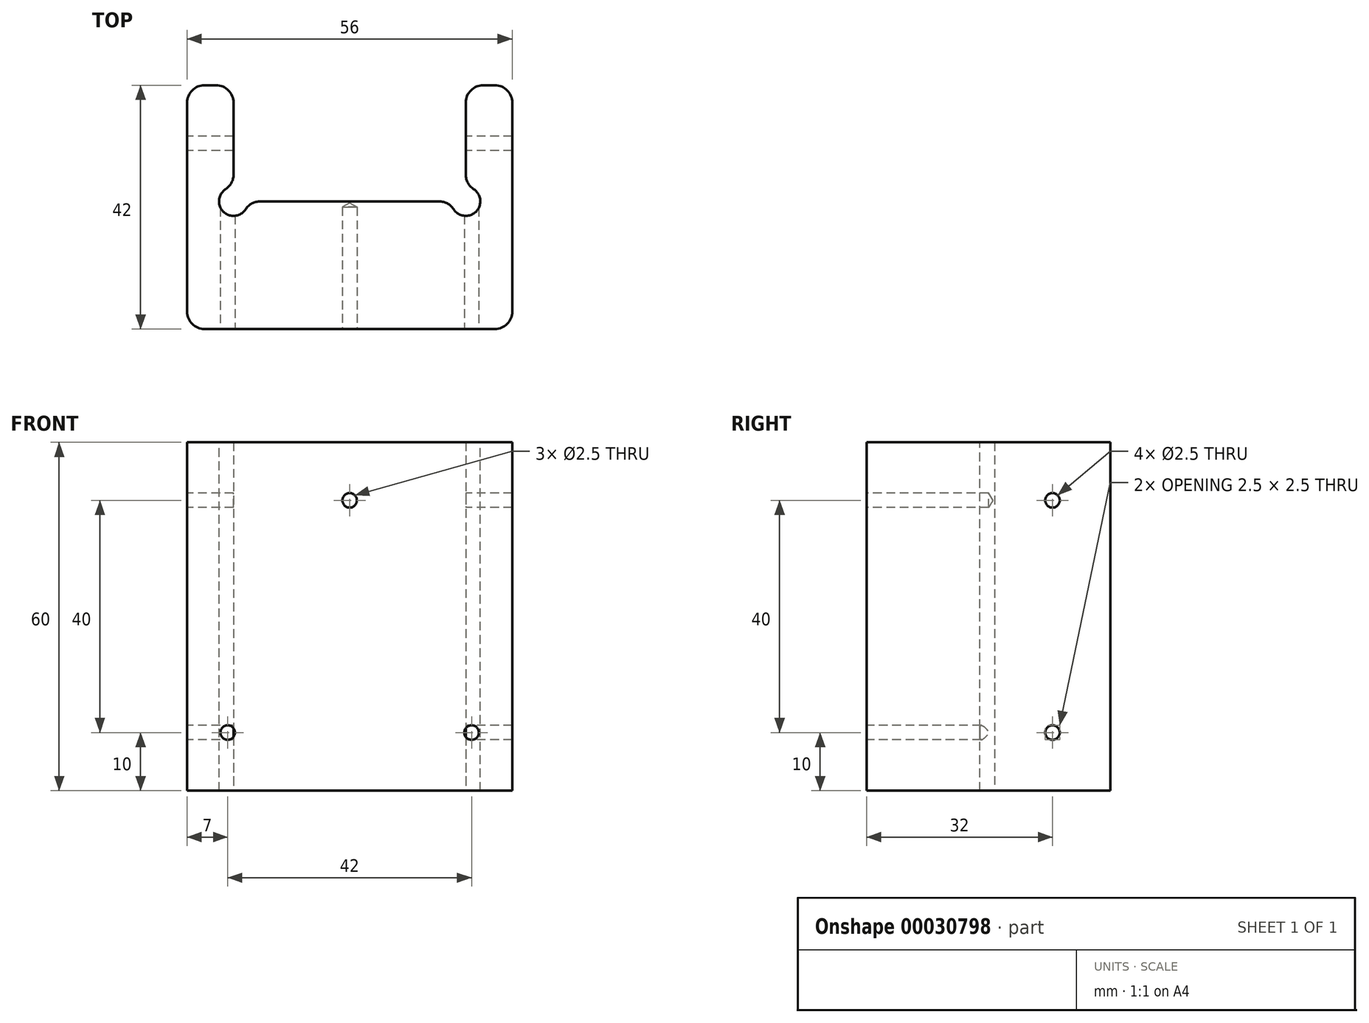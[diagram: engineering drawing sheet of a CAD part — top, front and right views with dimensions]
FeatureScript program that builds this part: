
annotation { "Feature Type Name" : "Feature", "Feature Type Description" : "" }
export const myFeature = defineFeature(function(context is Context, id is Id, definition is map)
    precondition{}
    {
        {
            var Q0;
            Q0=qCreatedBy(makeId("Top.planeOp"),FACE);
            var sketch = newSketch(context, id + "F0", { "sketchPlane" : qUnion([Q0])});
            skLineSegment(sketch, "E0.rect.bottom", {"start": v(-28, 21) * mm, "end": v(-20, 21) * mm});
            skLineSegment(sketch, "E0.rect.top", {"start": v(-28, -21) * mm, "end": v(28, -21) * mm});
            skLineSegment(sketch, "E0.rect.left", {"start": v(-28, 21) * mm, "end": v(-28, -21) * mm});
            skLineSegment(sketch, "E0.rect.right", {"start": v(28, 21) * mm, "end": v(28, -21) * mm});
            skPoint(sketch, "E0.rect.middle", {"position": v(0, 0) * mm});
            skLineSegment(sketch, "E1", {"start": v(-20, 21) * mm, "end": v(-20, 1) * mm});
            skLineSegment(sketch, "E2", {"start": v(-20, 1) * mm, "end": v(20, 1) * mm});
            skLineSegment(sketch, "E3", {"start": v(20, 1) * mm, "end": v(20, 21) * mm});
            skLineSegment(sketch, "E4.trimOffspring", {"start": v(20, 21) * mm, "end": v(28, 21) * mm});
            skSolve(sketch);
        }
        {
            var Q0;
            Q0 = qSketchRegion(id + "F0", true);
            extrude(context, id + "F1", {"entities" : qUnion([Q0]), "endBound" : BoundingType.SYMMETRIC, "depth" : 60 * mm});
        }
        {
            var Q0;
            Q0=makeQuery(id+"F1.opExtrude","SWEPT_FACE",FACE,{"disambiguationData":[OSD([sQuery(id+"F0.wireOp",EDGE,"E0.rect.left")])]});
            var sketch = newSketch(context, id + "F2", { "sketchPlane" : qUnion([Q0])});
            skPoint(sketch, "E5", {"position": v(-11, 20) * mm});
            skPoint(sketch, "E6", {"position": v(-11, -20) * mm});
            skLineSegment(sketch, "E7", {"start": v(-11, 20) * mm, "end": v(-11, -20) * mm, "construction": true});
            skLineSegment(sketch, "E8", {"start": v(-11, 0) * mm, "end": v(0, 0) * mm, "construction": true});
            skSolve(sketch);
        }
        {
            var Q0;
            Q0=sQuery(id+"F2.wireOp",VERTEX,"E5");
            var Q1;
            Q1=sQuery(id+"F2.wireOp",VERTEX,"E6");
            var Q2;
            Q2=makeQuery(id+"F1.opExtrude","SWEPT_BODY",BODY,{"disambiguationData":[OSD([sQuery(id+"F0.wireOp",EDGE,"E0.rect.bottom"),sQuery(id+"F0.wireOp",EDGE,"E0.rect.top"),sQuery(id+"F0.wireOp",EDGE,"E0.rect.left"),sQuery(id+"F0.wireOp",EDGE,"E0.rect.right"),sQuery(id+"F0.wireOp",EDGE,"E1"),sQuery(id+"F0.wireOp",EDGE,"E2"),sQuery(id+"F0.wireOp",EDGE,"E3"),sQuery(id+"F0.wireOp",EDGE,"E4.trimOffspring")])]});
            hole(context, id + "F3", {"style" : HoleStyle.SIMPLE, "holeDiameter" : 2.5 * mm, "endStyle" : HoleEndStyle.THROUGH, "locations" : qUnion([Q0, Q1]), "scope" : qUnion([Q2])});
        }
        {
            var Q0;
            Q0=makeQuery(id+"F1.opExtrude","SWEPT_FACE",FACE,{"disambiguationData":[OSD([sQuery(id+"F0.wireOp",EDGE,"E0.rect.top")])]});
            var sketch = newSketch(context, id + "F4", { "sketchPlane" : qUnion([Q0])});
            skPoint(sketch, "E9", {"position": v(0, 20) * mm});
            skPoint(sketch, "E10", {"position": v(-21, -20) * mm});
            skPoint(sketch, "E11", {"position": v(21, -20) * mm});
            skLineSegment(sketch, "E12", {"start": v(0, 20) * mm, "end": v(0, 0) * mm, "construction": true});
            skLineSegment(sketch, "E13", {"start": v(0, 0) * mm, "end": v(-21, -20) * mm, "construction": true});
            skLineSegment(sketch, "E14", {"start": v(0, 0) * mm, "end": v(21, -20) * mm, "construction": true});
            skLineSegment(sketch, "E15", {"start": v(0, 20) * mm, "end": v(-21, -20) * mm, "construction": true});
            skLineSegment(sketch, "E16", {"start": v(-21, -20) * mm, "end": v(21, -20) * mm, "construction": true});
            skLineSegment(sketch, "E17", {"start": v(21, -20) * mm, "end": v(0, 20) * mm, "construction": true});
            skLineSegment(sketch, "E18", {"start": v(0, 0) * mm, "end": v(0, -20) * mm, "construction": true});
            skSolve(sketch);
        }
        {
            var Q0;
            Q0=sQuery(id+"F4.wireOp",VERTEX,"E9");
            var Q1;
            Q1=sQuery(id+"F4.wireOp",VERTEX,"E10");
            var Q2;
            Q2=sQuery(id+"F4.wireOp",VERTEX,"E11");
            var Q3;
            Q3=makeQuery(id+"F1.opExtrude","SWEPT_BODY",BODY,{"disambiguationData":[OSD([sQuery(id+"F0.wireOp",EDGE,"E0.rect.bottom"),sQuery(id+"F0.wireOp",EDGE,"E0.rect.top"),sQuery(id+"F0.wireOp",EDGE,"E0.rect.left"),sQuery(id+"F0.wireOp",EDGE,"E0.rect.right"),sQuery(id+"F0.wireOp",EDGE,"E1"),sQuery(id+"F0.wireOp",EDGE,"E2"),sQuery(id+"F0.wireOp",EDGE,"E3"),sQuery(id+"F0.wireOp",EDGE,"E4.trimOffspring")])]});
            hole(context, id + "F5", {"style" : HoleStyle.SIMPLE, "holeDiameter" : 2.5 * mm, "endStyle" : HoleEndStyle.BLIND, "holeDepth" : 21 * mm, "locations" : qUnion([Q0, Q1, Q2]), "scope" : qUnion([Q3])});
        }
        {
            var Q0;
            Q0=makeQuery(id+"F1.opExtrude","SWEPT_EDGE",EDGE,{"disambiguationData":[OSD([sQuery(id+"F0.wireOp",EDGE,"E0.rect.top"),sQuery(id+"F0.wireOp",EDGE,"E0.rect.left")])]});
            var Q1;
            Q1=makeQuery(id+"F1.opExtrude","SWEPT_EDGE",EDGE,{"disambiguationData":[OSD([sQuery(id+"F0.wireOp",EDGE,"E0.rect.top"),sQuery(id+"F0.wireOp",EDGE,"E0.rect.right")])]});
            var Q2;
            Q2=makeQuery(id+"F1.opExtrude","SWEPT_EDGE",EDGE,{"disambiguationData":[OSD([sQuery(id+"F0.wireOp",EDGE,"E0.rect.bottom"),sQuery(id+"F0.wireOp",EDGE,"E0.rect.left")])]});
            var Q3;
            Q3=makeQuery(id+"F1.opExtrude","SWEPT_EDGE",EDGE,{"disambiguationData":[OSD([sQuery(id+"F0.wireOp",EDGE,"E0.rect.bottom"),sQuery(id+"F0.wireOp",EDGE,"E1")])]});
            var Q4;
            Q4=makeQuery(id+"F1.opExtrude","SWEPT_EDGE",EDGE,{"disambiguationData":[OSD([sQuery(id+"F0.wireOp",EDGE,"E3"),sQuery(id+"F0.wireOp",EDGE,"E4.trimOffspring")])]});
            var Q5;
            Q5=makeQuery(id+"F1.opExtrude","SWEPT_EDGE",EDGE,{"disambiguationData":[OSD([sQuery(id+"F0.wireOp",EDGE,"E0.rect.right"),sQuery(id+"F0.wireOp",EDGE,"E4.trimOffspring")])]});
            fillet(context, id + "F6", {"entities" : qUnion([Q0, Q1, Q2, Q3, Q4, Q5]), "radius" : 3 * mm, "tangentPropagation" : true, "allowEdgeOverflow" : false});
        }
        {
            var Q0;
            Q0=makeQuery(id+"F1.opExtrude","CAP_FACE",FACE,{"disambiguationData":[OSD([sQuery(id+"F0.wireOp",EDGE,"E0.rect.bottom"),sQuery(id+"F0.wireOp",EDGE,"E0.rect.top"),sQuery(id+"F0.wireOp",EDGE,"E0.rect.left"),sQuery(id+"F0.wireOp",EDGE,"E0.rect.right"),sQuery(id+"F0.wireOp",EDGE,"E1"),sQuery(id+"F0.wireOp",EDGE,"E2"),sQuery(id+"F0.wireOp",EDGE,"E3"),sQuery(id+"F0.wireOp",EDGE,"E4.trimOffspring")])],"isStart":false});
            var sketch = newSketch(context, id + "F7", { "sketchPlane" : qUnion([Q0])});
            skCircle(sketch, "E19", {"center": v(-20, 1) * mm, "radius": 2.5 * mm});
            skCircle(sketch, "E20", {"center": v(20, 1) * mm, "radius": 2.5 * mm});
            skSolve(sketch);
        }
        {
            var Q0;
            Q0 = qSketchRegion(id + "F7", true);
            extrude(context, id + "F8", {"entities" : qUnion([Q0]), "operationType" : NewBodyOperationType.REMOVE, "endBound" : BoundingType.THROUGH_ALL, "oppositeDirection" : true, "depth" : 25 * mm});
        }
        {
            var Q0;
            Q0=makeQuery(id+"F8.boolean.opBoolean","INTERSECT",EDGE,{"derivedFrom":[makeQuery(id+"F1.opExtrude","SWEPT_FACE",FACE,{"disambiguationData":[OSD([sQuery(id+"F0.wireOp",EDGE,"E2")])]}),makeQuery(id+"F8.opExtrude","SWEPT_FACE",FACE,{"disambiguationData":[OSD([sQuery(id+"F7.wireOp",EDGE,"E19")])]})]});
            var Q1;
            Q1=makeQuery(id+"F8.boolean.opBoolean","INTERSECT",EDGE,{"derivedFrom":[makeQuery(id+"F1.opExtrude","SWEPT_FACE",FACE,{"disambiguationData":[OSD([sQuery(id+"F0.wireOp",EDGE,"E1")])]}),makeQuery(id+"F8.opExtrude","SWEPT_FACE",FACE,{"disambiguationData":[OSD([sQuery(id+"F7.wireOp",EDGE,"E19")])]})]});
            var Q2;
            Q2=makeQuery(id+"F8.boolean.opBoolean","INTERSECT",EDGE,{"derivedFrom":[makeQuery(id+"F1.opExtrude","SWEPT_FACE",FACE,{"disambiguationData":[OSD([sQuery(id+"F0.wireOp",EDGE,"E2")])]}),makeQuery(id+"F8.opExtrude","SWEPT_FACE",FACE,{"disambiguationData":[OSD([sQuery(id+"F7.wireOp",EDGE,"E20")])]})]});
            var Q3;
            Q3=makeQuery(id+"F8.boolean.opBoolean","INTERSECT",EDGE,{"derivedFrom":[makeQuery(id+"F1.opExtrude","SWEPT_FACE",FACE,{"disambiguationData":[OSD([sQuery(id+"F0.wireOp",EDGE,"E3")])]}),makeQuery(id+"F8.opExtrude","SWEPT_FACE",FACE,{"disambiguationData":[OSD([sQuery(id+"F7.wireOp",EDGE,"E20")])]})]});
            fillet(context, id + "F9", {"entities" : qUnion([Q0, Q1, Q2, Q3]), "radius" : 3 * mm, "tangentPropagation" : true, "allowEdgeOverflow" : false});
        }
    });
